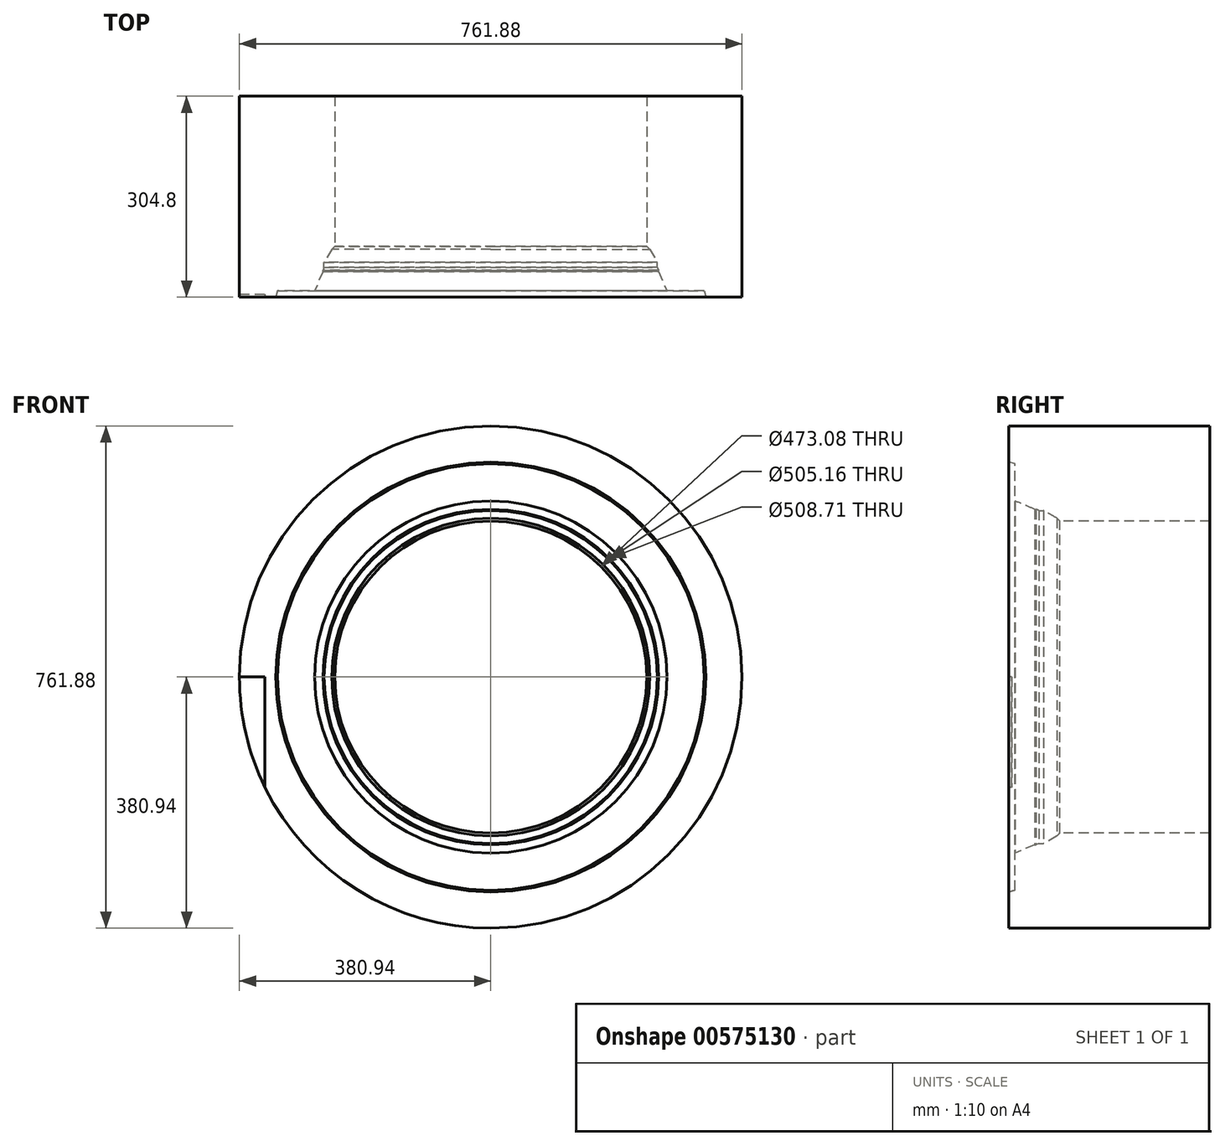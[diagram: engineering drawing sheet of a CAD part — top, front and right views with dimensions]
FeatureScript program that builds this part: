
annotation { "Feature Type Name" : "Feature", "Feature Type Description" : "" }
export const myFeature = defineFeature(function(context is Context, id is Id, definition is map)
    precondition{}
    {
        {
            var Q0;
            Q0=qCreatedBy(makeId("Front.planeOp"),FACE);
            var sketch = newSketch(context, id + "F0", { "sketchPlane" : qUnion([Q0])});
            skCircle(sketch, "E0", {"center": v(0, 0) * mm, "radius": 236.54 * mm});
            skCircle(sketch, "E1", {"center": v(0, 0) * mm, "radius": 380.94 * mm});
            skSolve(sketch);
        }
        {
            var Q0;
            Q0=qSketchRegion(id+"F0",true);
            extrude(context, id + "F1", {"entities" : qUnion([Q0]), "oppositeDirection" : true, "depth" : 304.8 * mm, "offsetDistance" : 25.4 * mm});
        }
        {
            var Q0;
            Q0=qCreatedBy(makeId("Right.planeOp"),FACE);
            var sketch = newSketch(context, id + "F2", { "sketchPlane" : qUnion([Q0])});
            skLineSegment(sketch, "E2", {"start": v(0, 0) * mm, "end": v(-223.81, 0) * mm});
            skPoint(sketch, "E3", {"position": v(0, 325.9) * mm});
            skLineSegment(sketch, "E4", {"start": v(9.52, 323.44) * mm, "end": v(9.53, 0) * mm});
            skLineSegment(sketch, "E5", {"start": v(0, 325.9) * mm, "end": v(9.53, 323.44) * mm});
            skLineSegment(sketch, "E6", {"start": v(0, 0) * mm, "end": v(9.53, 0) * mm});
            skLineSegment(sketch, "E7", {"start": v(0, 325.9) * mm, "end": v(-38.14, 325.9) * mm});
            skLineSegment(sketch, "E8", {"start": v(-38.14, 325.9) * mm, "end": v(0, -5.87) * mm});
            skSolve(sketch);
        }
        {
            var Q0;
            Q0=qSketchRegion(id+"F2",true);
            var Q1;
            Q1=sQuery(id+"F2.wireOp",EDGE,"E2");
            revolve(context, id + "F3", {"operationType" : NewBodyOperationType.REMOVE, "entities" : qUnion([Q0]), "axis" : qUnion([Q1]), "revolveType" : RevolveType.FULL, "oppositeDirection" : true});
        }
        {
            var Q0;
            Q0=qCreatedBy(makeId("Right.planeOp"),FACE);
            var sketch = newSketch(context, id + "F4", { "sketchPlane" : qUnion([Q0])});
            skPoint(sketch, "E9", {"position": v(9.52, 267) * mm});
            skLineSegment(sketch, "E10", {"start": v(9.52, 267) * mm, "end": v(39.3, 254.36) * mm});
            skLineSegment(sketch, "E11", {"start": v(41.25, 254.36) * mm, "end": v(39.3, 254.36) * mm});
            skLineSegment(sketch, "E12", {"start": v(41.25, 254.36) * mm, "end": v(45.44, 252.58) * mm});
            skLineSegment(sketch, "E13", {"start": v(45.44, 252.58) * mm, "end": v(52.7, 252.58) * mm});
            skLineSegment(sketch, "E14", {"start": v(52.7, 252.58) * mm, "end": v(72.8, 240.98) * mm});
            skLineSegment(sketch, "E15", {"start": v(72.8, 240.98) * mm, "end": v(83.79, 229.98) * mm});
            skLineSegment(sketch, "E16", {"start": v(9.52, 267) * mm, "end": v(-83.95, 267) * mm});
            skLineSegment(sketch, "E17", {"start": v(-83.95, 267) * mm, "end": v(-48.08, 188) * mm});
            skLineSegment(sketch, "E18", {"start": v(-48.08, 188) * mm, "end": v(83.79, 229.98) * mm});
            skSolve(sketch);
        }
        {
            var Q0;
            Q0=qSketchRegion(id+"F4",true);
            var Q1;
            Q1=makeQuery(id+"F1.opExtrude","SWEPT_FACE",FACE,{"disambiguationData":[OSD([sQuery(id+"F0.wireOp",EDGE,"E0")])]});
            revolve(context, id + "F5", {"operationType" : NewBodyOperationType.REMOVE, "entities" : qUnion([Q0]), "axis" : qUnion([Q1]), "revolveType" : RevolveType.FULL, "oppositeDirection" : true});
        }
        {
            var Q0;
            Q0=qCreatedBy(makeId("Top.planeOp"),FACE);
            var sketch = newSketch(context, id + "F6", { "sketchPlane" : qUnion([Q0])});
            skLineSegment(sketch, "E19.bottom", {"start": v(-395.47, -13.39) * mm, "end": v(-342.23, -13.39) * mm});
            skLineSegment(sketch, "E19.top", {"start": v(-395.47, 4.5) * mm, "end": v(-342.23, 4.5) * mm});
            skLineSegment(sketch, "E19.left", {"start": v(-395.47, -13.39) * mm, "end": v(-395.47, 4.5) * mm});
            skLineSegment(sketch, "E19.right", {"start": v(-342.23, -13.39) * mm, "end": v(-342.23, 4.5) * mm});
            skSolve(sketch);
        }
        {
            var Q0;
            Q0 = qSketchRegion(id + "F6", true);
            extrude(context, id + "F7", {"entities" : qUnion([Q0]), "operationType" : NewBodyOperationType.REMOVE, "oppositeDirection" : true, "depth" : 231.14 * mm, "offsetDistance" : 25.4 * mm});
        }
    });
